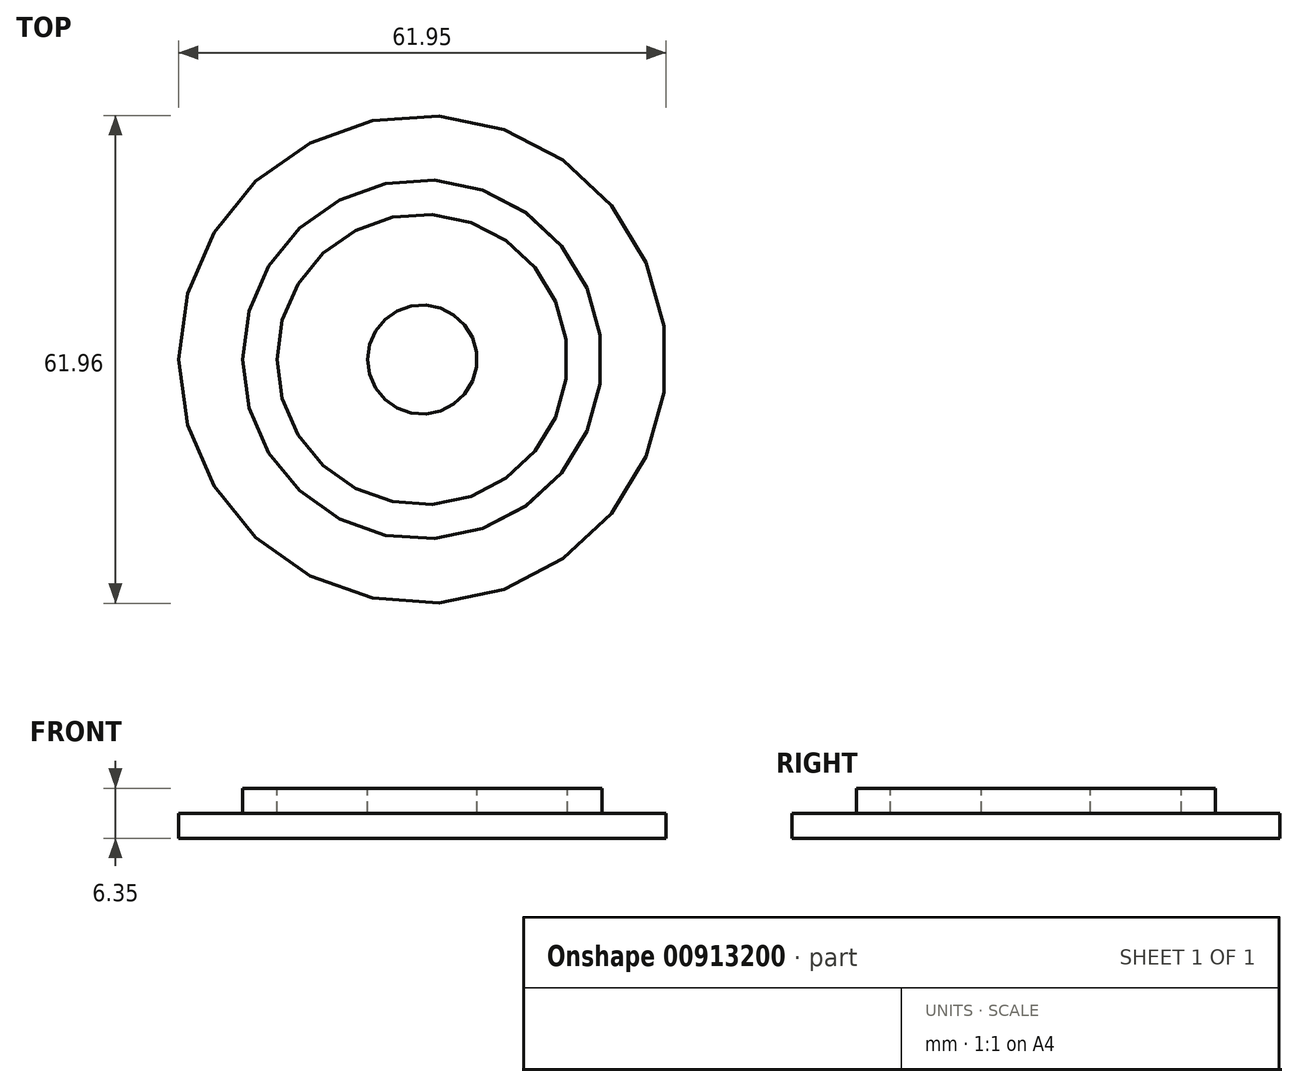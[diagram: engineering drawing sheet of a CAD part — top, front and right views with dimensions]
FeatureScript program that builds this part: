
annotation { "Feature Type Name" : "Feature", "Feature Type Description" : "" }
export const myFeature = defineFeature(function(context is Context, id is Id, definition is map)
    precondition{}
    {
        {
            var Q0;
            Q0=qCreatedBy(makeId("Front.planeOp"),FACE);
            var sketch = newSketch(context, id + "F0", { "sketchPlane" : qUnion([Q0])});
            skLineSegment(sketch, "E0", {"start": v(-57.66, -14.34) * mm, "end": v(-57.66, 49.43) * mm, "construction": true});
            skLineSegment(sketch, "E1", {"start": v(-57.66, 6.35) * mm, "end": v(-50.72, 6.35) * mm});
            skLineSegment(sketch, "E2", {"start": v(-39.2, 6.35) * mm, "end": v(-34.85, 6.35) * mm});
            skLineSegment(sketch, "E3", {"start": v(-26.68, 3.18) * mm, "end": v(-26.68, 0) * mm});
            skLineSegment(sketch, "E4", {"start": v(-26.68, 0) * mm, "end": v(-57.66, 0) * mm});
            skLineSegment(sketch, "E5", {"start": v(-57.66, 0) * mm, "end": v(-57.66, 6.35) * mm});
            skLineSegment(sketch, "E6", {"start": v(-50.72, 6.35) * mm, "end": v(-50.72, 3.18) * mm});
            skLineSegment(sketch, "E7", {"start": v(-39.2, 6.35) * mm, "end": v(-39.2, 3.18) * mm});
            skLineSegment(sketch, "E8", {"start": v(-34.85, 3.18) * mm, "end": v(-34.85, 6.35) * mm});
            skLineSegment(sketch, "E9", {"start": v(-50.72, 3.18) * mm, "end": v(-39.2, 3.18) * mm});
            skLineSegment(sketch, "E10", {"start": v(-34.85, 3.18) * mm, "end": v(-26.68, 3.18) * mm});
            skSolve(sketch);
        }
        {
            var Q0;
            Q0=makeQuery(id+"F0.imprint","IMPRINT",FACE,{"disambiguationData":[TD([[makeQuery(id+"F0.imprint","IMPRINT",EDGE,{"derivedFrom":sQuery(id+"F0.wireOp",EDGE,"E1")}),-1.0]])]});
            var Q1;
            Q1=sQuery(id+"F0.wireOp",EDGE,"E5");
            revolve(context, id + "F1", {"surfaceOperationType" : NewSurfaceOperationType.NEW, "entities" : qUnion([Q0]), "axis" : qUnion([Q1]), "revolveType" : RevolveType.FULL});
        }
    });
